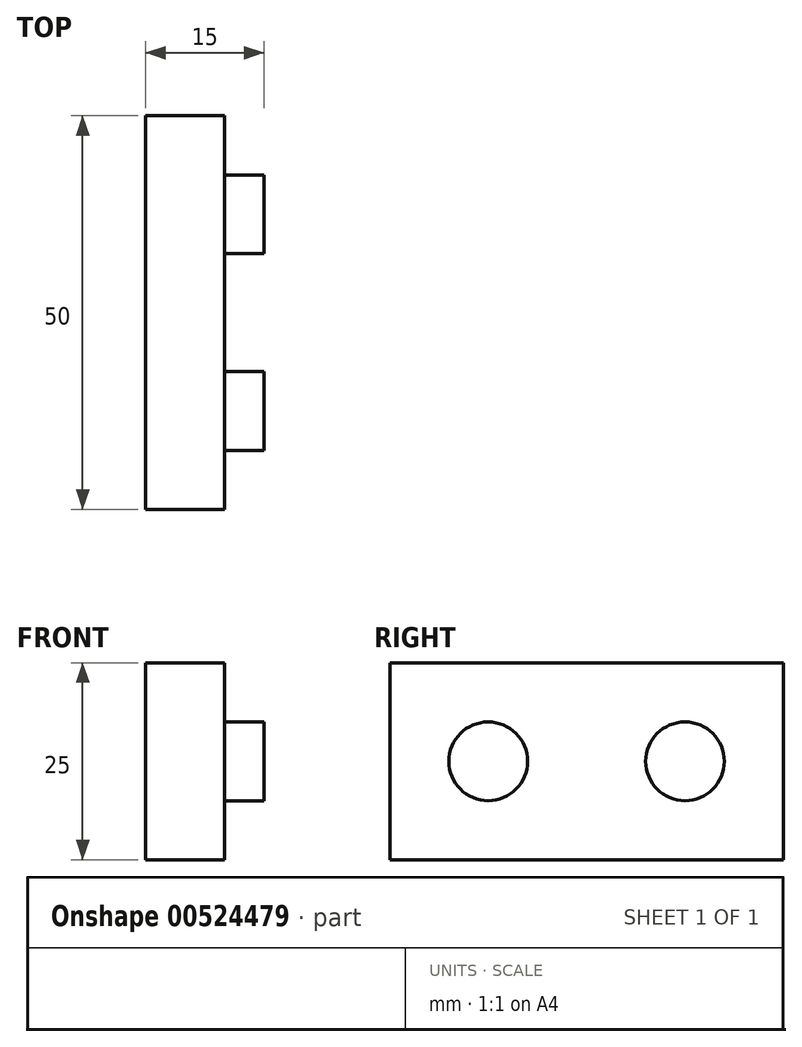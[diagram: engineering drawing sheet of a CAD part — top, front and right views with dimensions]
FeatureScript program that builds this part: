
annotation { "Feature Type Name" : "Feature", "Feature Type Description" : "" }
export const myFeature = defineFeature(function(context is Context, id is Id, definition is map)
    precondition{}
    {
        {
            var Q0;
            Q0=qCreatedBy(makeId("Front.planeOp"),FACE);
            var sketch = newSketch(context, id + "F0", { "sketchPlane" : qUnion([Q0])});
            skLineSegment(sketch, "E0.bottom", {"start": v(25, 12.5) * mm, "end": v(-25, 12.5) * mm});
            skLineSegment(sketch, "E0.top", {"start": v(25, -12.5) * mm, "end": v(-25, -12.5) * mm});
            skLineSegment(sketch, "E0.left", {"start": v(25, 12.5) * mm, "end": v(25, -12.5) * mm});
            skLineSegment(sketch, "E0.right", {"start": v(-25, 12.5) * mm, "end": v(-25, -12.5) * mm});
            skPoint(sketch, "E0.middle", {"position": v(0, 0) * mm});
            skSolve(sketch);
        }
        {
            var Q0;
            Q0 = qSketchRegion(id + "F0", true);
            extrude(context, id + "F1", {"entities" : qUnion([Q0]), "depth" : 10 * mm, "offsetDistance" : 25 * mm});
        }
        {
            var Q0;
            Q0=makeQuery(id+"F1.opExtrude","CAP_FACE",FACE,{"disambiguationData":[OSD([sQuery(id+"F0.wireOp",EDGE,"E0.bottom"),sQuery(id+"F0.wireOp",EDGE,"E0.top"),sQuery(id+"F0.wireOp",EDGE,"E0.left"),sQuery(id+"F0.wireOp",EDGE,"E0.right")])],"isStart":false});
            var sketch = newSketch(context, id + "F2", { "sketchPlane" : qUnion([Q0])});
            skLineSegment(sketch, "E1", {"start": v(0, 0) * mm, "end": v(-25, 0) * mm, "construction": true});
            skLineSegment(sketch, "E2", {"start": v(0, 0) * mm, "end": v(25, 0) * mm, "construction": true});
            skLineSegment(sketch, "E3", {"start": v(-12.5, 0) * mm, "end": v(-12.5, 12.5) * mm, "construction": true});
            skLineSegment(sketch, "E4", {"start": v(12.5, 0) * mm, "end": v(12.5, 12.5) * mm, "construction": true});
            skCircle(sketch, "E5", {"center": v(-12.5, 0) * mm, "radius": 5 * mm});
            skCircle(sketch, "E6", {"center": v(12.5, 0) * mm, "radius": 5 * mm});
            skSolve(sketch);
        }
        {
            var Q0;
            Q0 = qSketchRegion(id + "F2", true);
            extrude(context, id + "F3", {"entities" : qUnion([Q0]), "operationType" : NewBodyOperationType.ADD, "depth" : 5 * mm, "offsetDistance" : 25 * mm});
        }
        {
            var Q0;
            Q0=makeQuery(id+"F1.opExtrude","SWEPT_BODY",BODY,{"disambiguationData":[OSD([sQuery(id+"F0.wireOp",EDGE,"E0.bottom"),sQuery(id+"F0.wireOp",EDGE,"E0.top"),sQuery(id+"F0.wireOp",EDGE,"E0.left"),sQuery(id+"F0.wireOp",EDGE,"E0.right")])]});
            var Q1;
            Q1=makeQuery(id+"F1.opExtrude","CAP_EDGE",EDGE,{"disambiguationData":[OSD([sQuery(id+"F0.wireOp",EDGE,"E0.right")])],"isStart":true});
            transform(context, id + "F4", {"entities" : qUnion([Q0]), "transformType" : TransformType.ROTATION, "transformAxis" : qUnion([Q1]), "angle" : 270 * degree, "makeCopy" : false});
        }
    });
